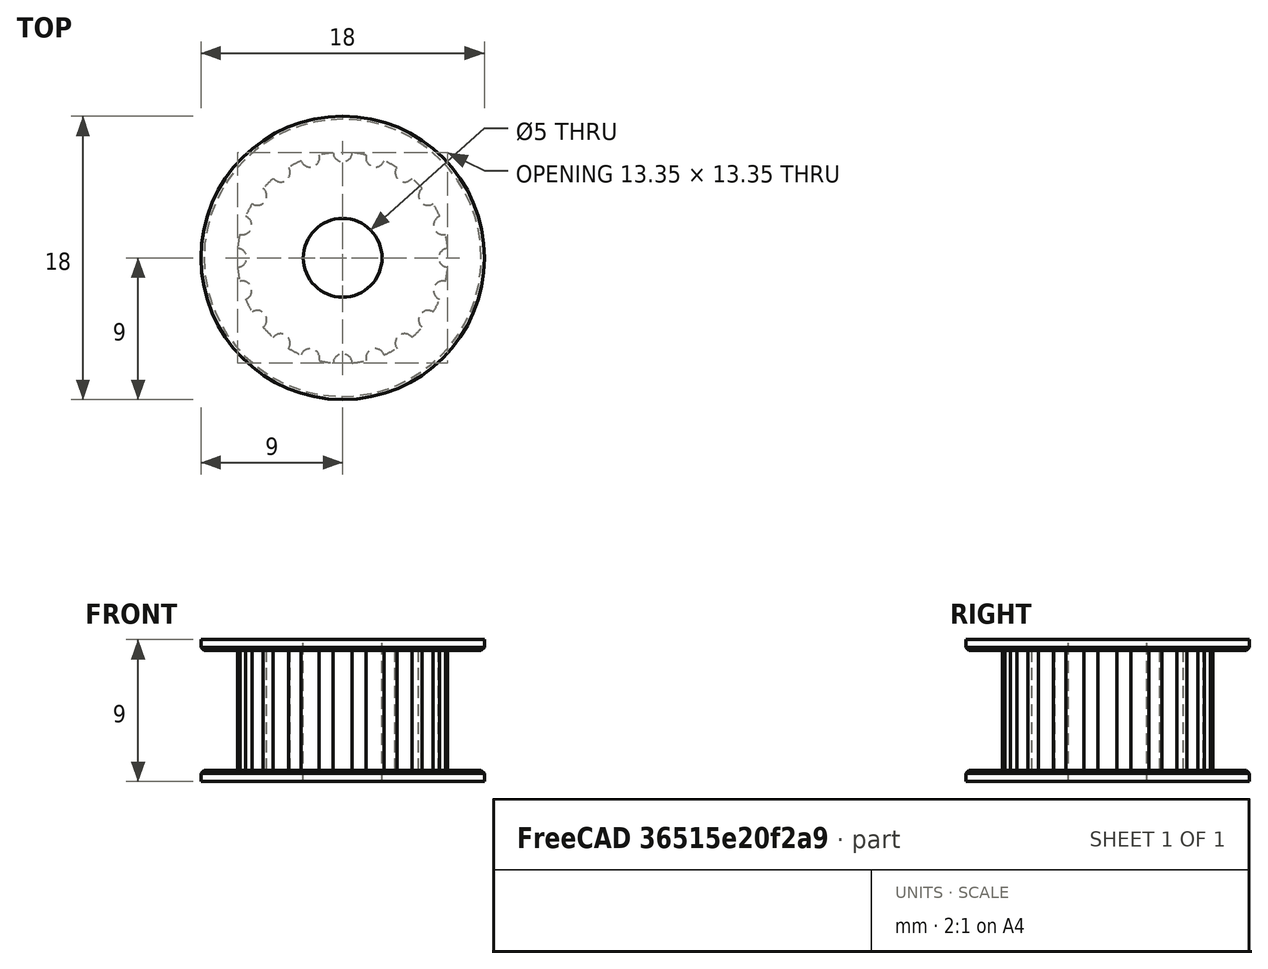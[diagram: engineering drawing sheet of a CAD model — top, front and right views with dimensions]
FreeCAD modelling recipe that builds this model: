
FCSTD DOCUMENT  (FreeCAD 0.16R6706 (Git))
Label: GT2Pulley-V3
License: CC-BY 3.0
LicenseURL: http://creativecommons.org/licenses/by/3.0/
objects: Part::Cylinder×5, Part::Cut×2, Part::Chamfer×2, Part::FeaturePython×1, Part::MultiFuse×1, Part::Feature×1
note: 12 computed .brp shape members not serialized (recipe doc carries the construction recipe); baked Part::Feature solids carry a one-line shape summary decoded from their .brp

FEATURE [Part::Cylinder] Cylinder  label="Cilindro"
  Angle = 360
  Height = 7.6
  Placement = pos=(6.7,0,0) rot=(0,0,1;0rad)
  Radius = 0.6
FEATURE [Part::FeaturePython] Array  # Draft array (typed FeaturePython)
  Angle = 360
  ArrayType = 1
  Axis = (0,0,1)
  Base = -> Cylinder
  Center = (0,0,0)
  IntervalX = (1,0,0)
  IntervalY = (0,1,0)
  IntervalZ = (0,0,1)
  NumberPolar = 20
  NumberX = 2
  NumberY = 2
  NumberZ = 1
FEATURE [Part::Cylinder] Cylinder001  label="Cilindro001"
  Angle = 360
  Height = 7.6
  Radius = 6.7
FEATURE [Part::Cut] Cut
  Base = -> Cylinder001
  Placement = pos=(0,0,0.7) rot=(0,0,1;0rad)
  Tool = -> Array
FEATURE [Part::Cylinder] Cylinder002  label="Cilindro002"
  Angle = 360
  Height = 0.7
  Radius = 9
FEATURE [Part::Cylinder] Cylinder003  label="Cilindro003"
  Angle = 360
  Height = 0.7
  Placement = pos=(0,0,8.3) rot=(0,0,1;0rad)
  Radius = 9
FEATURE [Part::Chamfer] Chamfer
  Base = -> Cylinder002
  Edges = 1 edges r=0.2: [Edge1]
FEATURE [Part::Chamfer] Chamfer001
  Base = -> Cylinder003
  Edges = 1 edges r=0.2: [Edge3]
FEATURE [Part::MultiFuse] Fusion
  Shapes = -> [Cut,Chamfer,Chamfer001]
FEATURE [Part::Cylinder] Cylinder004  label="Cilindro004"
  Angle = 360
  Height = 28.6
  Placement = pos=(0,0,-6) rot=(0,0,1;0rad)
  Radius = 2.5
FEATURE [Part::Cut] Cut001
  Base = -> Fusion
  Tool = -> Cylinder004
FEATURE [Part::Feature] Cut001001  label="GT2Pulley"
  shape: bbox 18 x 18 x 9 mm, 49 faces (baked)
